# Revit family: TYCO-FPP-Zettler-DIM800 detector input monitor module
name_source: partatom
category: Electrical Fixtures
revit_build: Autodesk Revit 2014 (Build: 20130308_1515(x64)
units: mm (PartAtom-declared; Revit-internal decimal feet)

## types (1)
- TYCO-FPP-Zettler-DIM800 detector input monitor module
    Alarm Current = 30 to 50mA
    Alarm State Current = 280μA
    Ambient Temperature = –25°C to +70°C
–25°C to +70°C
    Current per Circuit = .5mA
    Description = The DIM800 Addressable Detector Input Module interfaces
two conventional detector circuits onto the MX addressable
loop.
    Detector EOL = 4k7 Ohm
    Detector Load = 3mA (max. per input)
    Front Cover = Yes
    Keynote = Interface up to 2 circuits of
conventional detectors
    Length = 61 mm
    Loop Voltage = 20V to 40Vdc
    Manufacturer = Tyco
    Model = Zettler-555.800.012
    PCB = PCB
    Quiescent Current = 280μA
280μA
    Rear Cover = Yes
    Relative Humidity = 10% to 95%
    Storage Temperature = –40°C to +80°C
    Type Comments = The CIM800 is a flexible addressable input-monitoring
device that fits in the standard ancillary housings.
    URL = https://www.tycosafetyproducts-anz.com
    Width = 84 mm
    Wire Size (maximum) = 2.5sq. mm

## geometry (parser evidence)
native form markers: Sweep x4
no freeform markers — native parametric forms only
